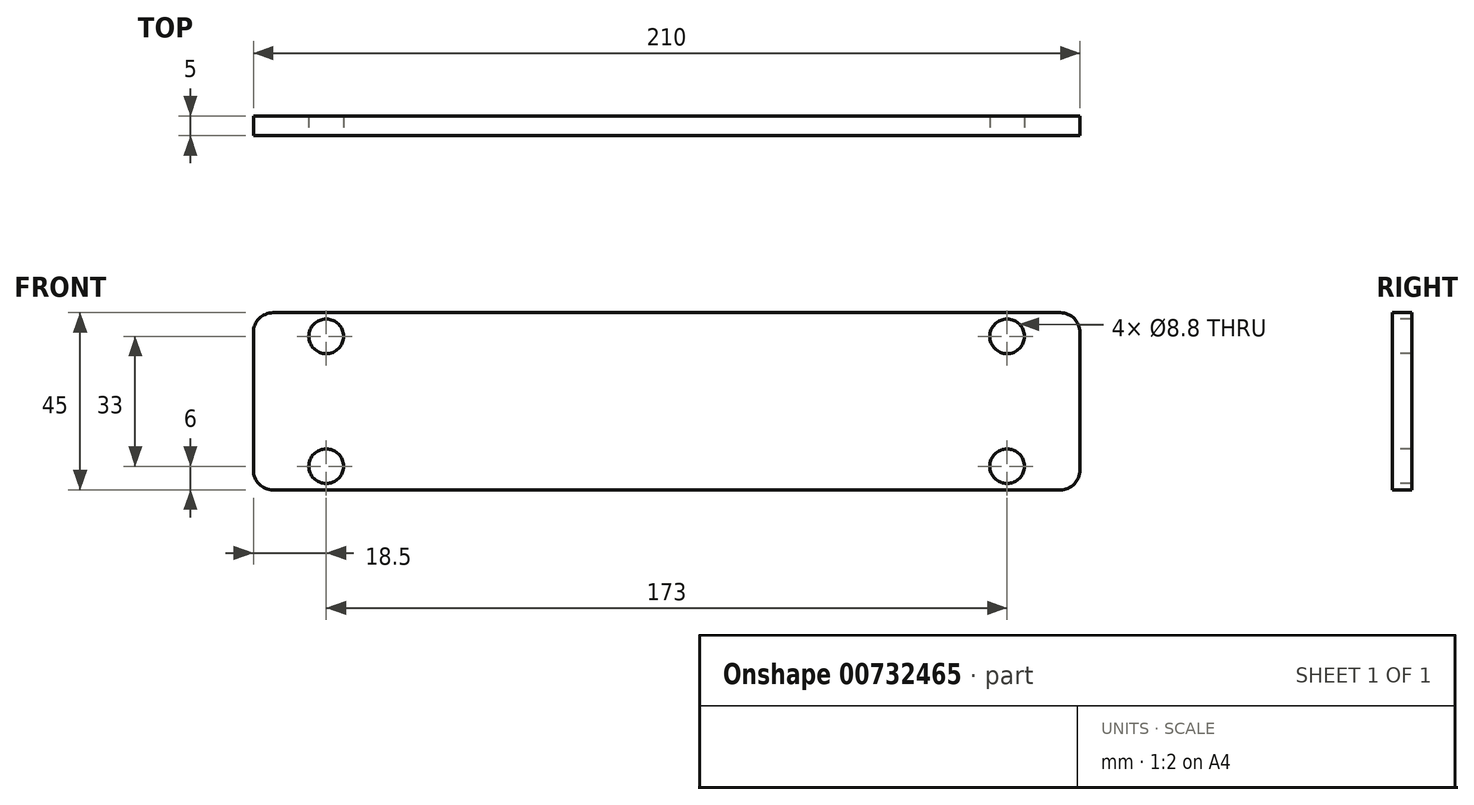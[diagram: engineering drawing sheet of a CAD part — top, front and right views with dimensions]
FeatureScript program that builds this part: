
annotation { "Feature Type Name" : "Feature", "Feature Type Description" : "" }
export const myFeature = defineFeature(function(context is Context, id is Id, definition is map)
    precondition{}
    {
        {
            var Q0;
            Q0=qCreatedBy(makeId("Front.planeOp"),FACE);
            var sketch = newSketch(context, id + "F0", { "sketchPlane" : qUnion([Q0])});
            skLineSegment(sketch, "E0.bottom", {"start": v(0, 0) * mm, "end": v(210, 0) * mm});
            skLineSegment(sketch, "E0.top", {"start": v(0, 45) * mm, "end": v(210, 45) * mm});
            skLineSegment(sketch, "E0.left", {"start": v(0, 0) * mm, "end": v(0, 45) * mm});
            skLineSegment(sketch, "E0.right", {"start": v(210, 0) * mm, "end": v(210, 45) * mm});
            skSolve(sketch);
        }
        {
            var Q0;
            Q0=makeQuery(id+"F0.imprint","IMPRINT",FACE,{"disambiguationData":[TD([[makeQuery(id+"F0.imprint","IMPRINT",EDGE,{"derivedFrom":sQuery(id+"F0.wireOp",EDGE,"E0.bottom")}),1.0]])]});
            extrude(context, id + "F1", {"entities" : qUnion([Q0]), "depth" : 5 * mm, "offsetDistance" : 25 * mm});
        }
        {
            var Q0;
            Q0=makeQuery(id+"F1.opExtrude","CAP_FACE",FACE,{"disambiguationData":[OSD([sQuery(id+"F0.wireOp",EDGE,"E0.bottom"),sQuery(id+"F0.wireOp",EDGE,"E0.top"),sQuery(id+"F0.wireOp",EDGE,"E0.left"),sQuery(id+"F0.wireOp",EDGE,"E0.right")])],"isStart":false});
            var sketch = newSketch(context, id + "F2", { "sketchPlane" : qUnion([Q0])});
            skPoint(sketch, "E1", {"position": v(18.5, 39) * mm});
            skPoint(sketch, "E2.0.1.0", {"position": v(18.5, 6) * mm});
            skPoint(sketch, "E2.1.0.0", {"position": v(191.5, 39) * mm});
            skPoint(sketch, "E2.1.1.0", {"position": v(191.5, 6) * mm});
            skLineSegment(sketch, "E2.direction1", {"start": v(18.5, 39) * mm, "end": v(191.5, 39) * mm, "construction": true});
            skLineSegment(sketch, "E2.direction2", {"start": v(18.5, 39) * mm, "end": v(18.5, 6) * mm, "construction": true});
            skSolve(sketch);
        }
        {
            var Q0;
            Q0=sQuery(id+"F2.wireOp",VERTEX,"E1");
            var Q1;
            Q1=sQuery(id+"F2.wireOp",VERTEX,"E2.0.1.0");
            var Q2;
            Q2=sQuery(id+"F2.wireOp",VERTEX,"E2.1.0.0");
            var Q3;
            Q3=sQuery(id+"F2.wireOp",VERTEX,"E2.1.1.0");
            var Q4;
            Q4=makeQuery(id+"F1.opExtrude","SWEPT_BODY",BODY,{"disambiguationData":[OSD([sQuery(id+"F0.wireOp",EDGE,"E0.bottom"),sQuery(id+"F0.wireOp",EDGE,"E0.top"),sQuery(id+"F0.wireOp",EDGE,"E0.left"),sQuery(id+"F0.wireOp",EDGE,"E0.right")])]});
            hole(context, id + "F3", {"style" : HoleStyle.SIMPLE, "endStyle" : HoleEndStyle.THROUGH, "standardTappedOrClearance" : lookupTablePath({ "standard" : "ISO", "fit" : "Normal", "size" : "M8", "type" : "Clearance" }), "standardBlindInLast" : lookupTablePath({ "fit" : "Standard", "standard" : "ISO", "size" : "M8", "type" : "Clearance" }), "holeDiameter" : 8.8 * mm, "majorDiameter" : 6 * mm, "tappedDepth" : 20 * mm, "tapClearance" : 3, "startFromSketch" : true, "locations" : qUnion([Q0, Q1, Q2, Q3]), "scope" : qUnion([Q4])});
        }
        {
            var Q0;
            Q0=makeQuery(id+"F1.opExtrude","SWEPT_EDGE",EDGE,{"disambiguationData":[OSD([sQuery(id+"F0.wireOp",EDGE,"E0.top"),sQuery(id+"F0.wireOp",EDGE,"E0.left")])]});
            var Q1;
            Q1=makeQuery(id+"F1.opExtrude","SWEPT_EDGE",EDGE,{"disambiguationData":[OSD([sQuery(id+"F0.wireOp",EDGE,"E0.bottom"),sQuery(id+"F0.wireOp",EDGE,"E0.left")])]});
            var Q2;
            Q2=makeQuery(id+"F1.opExtrude","SWEPT_EDGE",EDGE,{"disambiguationData":[OSD([sQuery(id+"F0.wireOp",EDGE,"E0.bottom"),sQuery(id+"F0.wireOp",EDGE,"E0.right")])]});
            var Q3;
            Q3=makeQuery(id+"F1.opExtrude","SWEPT_EDGE",EDGE,{"disambiguationData":[OSD([sQuery(id+"F0.wireOp",EDGE,"E0.top"),sQuery(id+"F0.wireOp",EDGE,"E0.right")])]});
            fillet(context, id + "F4", {"entities" : qUnion([Q0, Q1, Q2, Q3]), "radius" : 5 * mm, "tangentPropagation" : true, "allowEdgeOverflow" : false});
        }
    });
